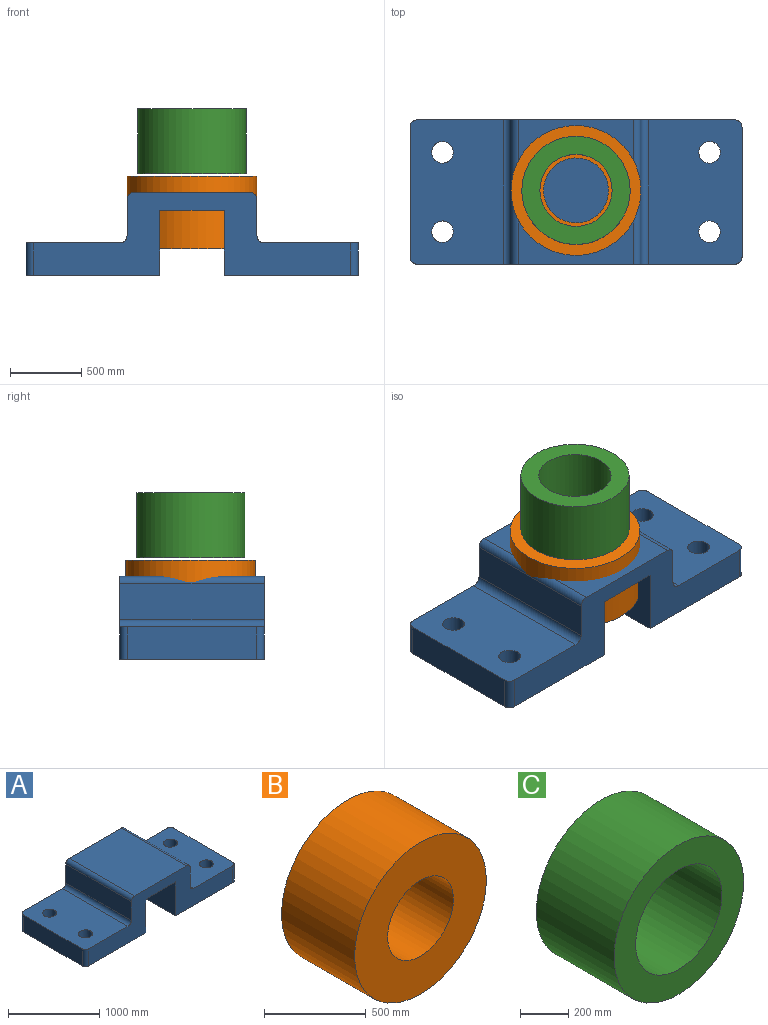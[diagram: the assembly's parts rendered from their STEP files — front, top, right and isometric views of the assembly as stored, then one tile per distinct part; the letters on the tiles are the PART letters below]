
ASSEMBLY  parts=3 mates=2
PART A: 26 faces, bbox 2336.8x1016x584.2 mm
  f0: plane 1016x939.8mm, normal (0,0,-1), area 917246.2mm2, adj f1,f11,f12,f13,f20,f21,f24,f25
  f1: plane 1016x457.2mm, normal (1,0,0), area 464515.2mm2, adj f0,f2,f12,f13
  f2: plane 1016x457.2mm, normal (0,0,-1), area 464515.2mm2, adj f1,f3,f12,f13
  f3: plane 1016x457.2mm, normal (-1,0,0), area 464515.2mm2, adj f2,f4,f12,f13
  f4: plane 1016x939.8mm, normal (0,0,-1), area 917246.2mm2, adj f3,f5,f12,f13,f14,f19,f22,f23
  f5: plane 914.4x228.6mm, normal (1,0,0), area 209031.8mm2, adj f4,f6,f14,f19
  f6: plane 1016x660.4mm, normal (0,0,1), area 633375.8mm2, adj f5,f12,f13,f14,f15,f19,f22,f23
  f7: plane 1016x254mm, normal (1,0,0), area 258064mm2, adj f12,f13,f15,f16
  f8: plane 1016x812.8mm, normal (0,0,1), area 825804.8mm2, adj f12,f13,f16,f17
  f9: plane 1016x254mm, normal (-1,0,0), area 258064mm2, adj f12,f13,f17,f18
  f10: plane 1016x660.4mm, normal (0,0,1), area 633375.8mm2, adj f11,f12,f13,f18,f20,f21,f24,f25
  f11: plane 914.4x228.6mm, normal (-1,0,0), area 209031.8mm2, adj f0,f10,f20,f21
  f12: plane 2235.2x584.2mm, normal (0,-1,0), area 627095.5mm2, adj f0,f1,f2,f3,f4,f6,f7,f8
  f13: plane 2235.2x584.2mm, normal (0,1,0), area 627095.5mm2, adj f0,f1,f2,f3,f4,f6,f7,f8
  f14: cylinder r=50.8mm len=228.6mm, axis (0,0,-1), area 18241.5mm2, adj f4,f5,f6,f12
  f15: cylinder r=50.8mm len=1016mm, axis (0,-1,0), area 81073.2mm2, adj f6,f7,f12,f13
  f16: cylinder r=50.8mm len=1016mm, axis (0,1,0), area 81073.2mm2, adj f7,f8,f12,f13
  f17: cylinder r=50.8mm len=1016mm, axis (0,1,0), area 81073.2mm2, adj f8,f9,f12,f13
  f18: cylinder r=50.8mm len=1016mm, axis (0,1,0), area 81073.2mm2, adj f9,f10,f12,f13
  f19: cylinder r=50.8mm len=228.6mm, axis (0,0,1), area 18241.5mm2, adj f4,f5,f6,f13
  f20: cylinder r=50.8mm len=228.6mm, axis (0,0,-1), area 18241.5mm2, adj f0,f10,f11,f13
  f21: cylinder r=50.8mm len=228.6mm, axis (0,0,1), area 18241.5mm2, adj f0,f10,f11,f12
  f22: cylinder r=76.2mm len=228.6mm, axis (0,0,1), area 109448.8mm2, adj f4,f6
  f23: cylinder r=76.2mm len=228.6mm, axis (0,0,1), area 109448.8mm2, adj f4,f6
  f24: cylinder r=76.2mm len=228.6mm, axis (0,0,1), area 109448.8mm2, adj f0,f10
  f25: cylinder r=76.2mm len=228.6mm, axis (0,0,1), area 109448.8mm2, adj f0,f10
PART B: 4 faces, bbox 914.4x508x914.4 mm
  f0: cylinder r=228.6mm len=508mm, axis (0,1,0), area 729658.8mm2, adj f2,f3
  f1: cylinder r=457.2mm len=914.4mm, axis (0,1,0), area 1459317.5mm2, adj f2,f3
  f2: plane 914.4x914.4mm, normal (0,-1,0), area 492519.7mm2, adj f0,f1
  f3: plane 914.4x914.4mm, normal (0,1,0), area 492519.7mm2, adj f0,f1
PART C: 4 faces, bbox 762x457.2x762 mm
  f0: cylinder r=254mm len=508mm, axis (0,1,0), area 729658.8mm2, adj f2,f3
  f1: cylinder r=381mm len=762mm, axis (0,1,0), area 1094488.2mm2, adj f2,f3
  f2: plane 762x762mm, normal (0,-1,0), area 253353.7mm2, adj f0,f1
  f3: plane 762x762mm, normal (0,1,0), area 253353.7mm2, adj f0,f1
PLACE A t=(-153.29,618.08,-150.42)mm
PLACE B rot(axis=(-1,0,0),90deg) t=(-1321.69,120.24,37.54)mm
PLACE C rot(axis=(0.58,0.58,0.58),120deg) t=(-1321.69,120.24,1023.06)mm
MATE parallel B.f0 <-> A.f8  axis (0,0,1) through (-1321.69,120.24,545.54)mm
MATE parallel C.f0 <-> B.f0  axis (0,0,1) through (-1321.69,120.24,1023.06)mm
